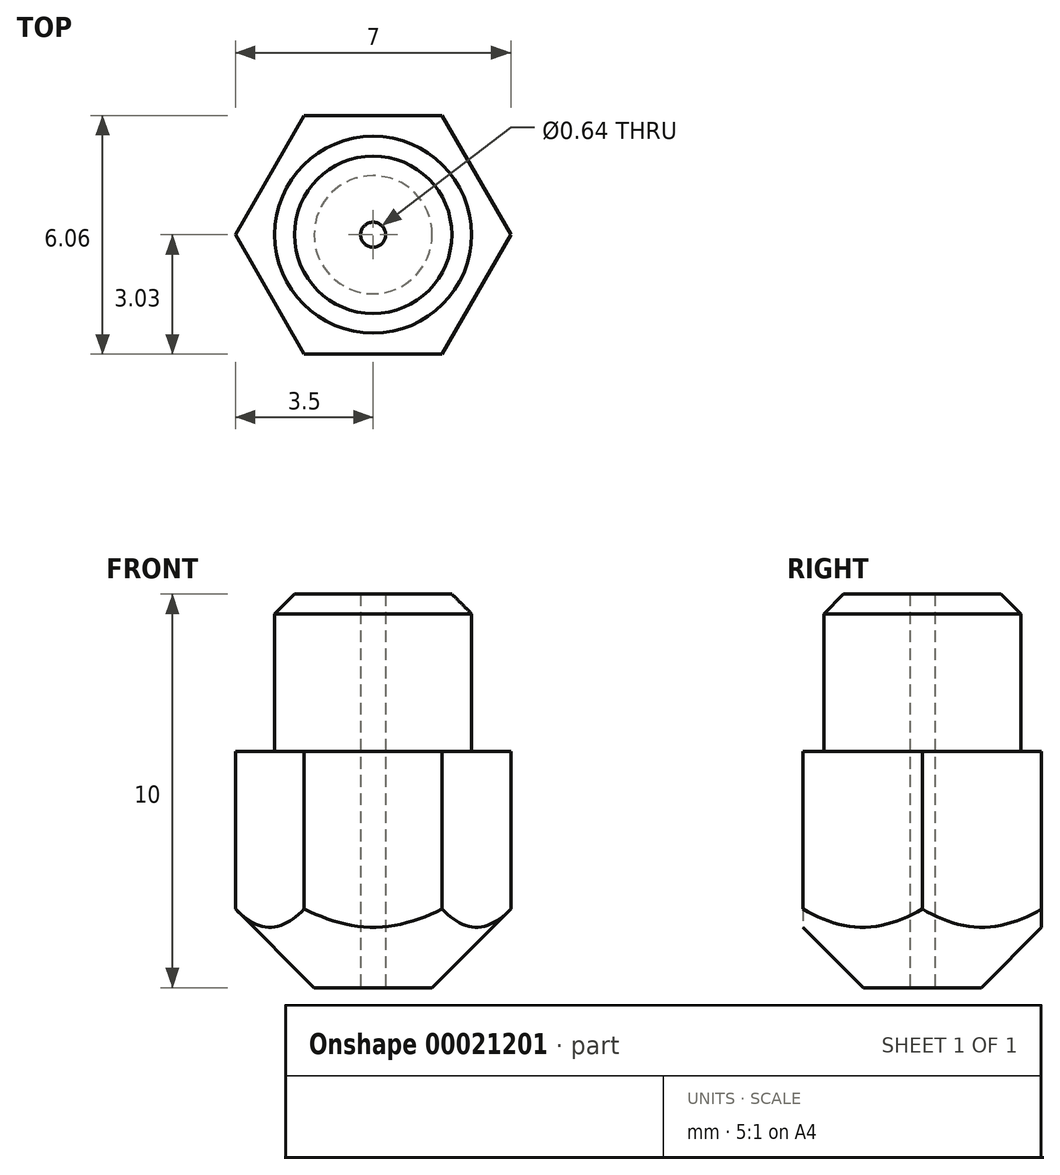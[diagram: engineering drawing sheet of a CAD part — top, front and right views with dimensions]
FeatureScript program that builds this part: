
annotation { "Feature Type Name" : "Feature", "Feature Type Description" : "" }
export const myFeature = defineFeature(function(context is Context, id is Id, definition is map)
    precondition{}
    {
        {
            var Q0;
            Q0=qCreatedBy(makeId("Top.planeOp"),FACE);
            var sketch = newSketch(context, id + "F0", { "sketchPlane" : qUnion([Q0])});
            skCircle(sketch, "E0.cCircle", {"center": v(0, 0) * mm, "radius": 3.03 * mm, "construction": true});
            skLineSegment(sketch, "E0.0", {"start": v(1.75, -3.03) * mm, "end": v(-1.75, -3.03) * mm});
            skLineSegment(sketch, "E0.1", {"start": v(-1.75, -3.03) * mm, "end": v(-3.5, 0) * mm});
            skLineSegment(sketch, "E0.2", {"start": v(-3.5, 0) * mm, "end": v(-1.75, 3.03) * mm});
            skLineSegment(sketch, "E0.3", {"start": v(-1.75, 3.03) * mm, "end": v(1.75, 3.03) * mm});
            skLineSegment(sketch, "E0.4", {"start": v(1.75, 3.03) * mm, "end": v(3.5, 0) * mm});
            skLineSegment(sketch, "E0.5", {"start": v(3.5, 0) * mm, "end": v(1.75, -3.03) * mm});
            skPoint(sketch, "E0.0.midPoint", {"position": v(0, -3.03) * mm});
            skSolve(sketch);
        }
        {
            var Q0;
            Q0=qSketchRegion(id+"F0",true);
            extrude(context, id + "F1", {"entities" : qUnion([Q0]), "depth" : 6 * mm});
        }
        {
            var Q0;
            Q0=qCreatedBy(makeId("Front.planeOp"),FACE);
            var sketch = newSketch(context, id + "F2", { "sketchPlane" : qUnion([Q0])});
            skLineSegment(sketch, "E1", {"start": v(1.5, 0) * mm, "end": v(3.5, 2) * mm});
            skLineSegment(sketch, "E2", {"start": v(3.5, 2) * mm, "end": v(3.5, 0) * mm});
            skLineSegment(sketch, "E3", {"start": v(3.5, 0) * mm, "end": v(1.5, 0) * mm});
            skLineSegment(sketch, "E4", {"start": v(0, 0) * mm, "end": v(0, 3.2) * mm, "construction": true});
            skSolve(sketch);
        }
        {
            var Q0;
            Q0=qSketchRegion(id+"F2",true);
            var Q1;
            Q1=sQuery(id+"F2.wireOp",EDGE,"E4");
            revolve(context, id + "F3", {"operationType" : NewBodyOperationType.REMOVE, "entities" : qUnion([Q0]), "axis" : qUnion([Q1]), "revolveType" : RevolveType.FULL, "oppositeDirection" : true});
        }
        {
            var Q0;
            Q0=makeQuery(id+"F1.opExtrude","CAP_FACE",FACE,{"disambiguationData":[OSD([sQuery(id+"F0.wireOp",EDGE,"E0.0"),sQuery(id+"F0.wireOp",EDGE,"E0.1"),sQuery(id+"F0.wireOp",EDGE,"E0.2"),sQuery(id+"F0.wireOp",EDGE,"E0.3"),sQuery(id+"F0.wireOp",EDGE,"E0.4"),sQuery(id+"F0.wireOp",EDGE,"E0.5")])],"isStart":false});
            var sketch = newSketch(context, id + "F4", { "sketchPlane" : qUnion([Q0])});
            skCircle(sketch, "E5", {"center": v(0, 0) * mm, "radius": 2.5 * mm});
            skSolve(sketch);
        }
        {
            var Q0;
            Q0=qSketchRegion(id+"F4",true);
            extrude(context, id + "F5", {"entities" : qUnion([Q0]), "operationType" : NewBodyOperationType.ADD, "depth" : 4 * mm});
        }
        {
            var Q0;
            Q0=makeQuery(id+"F5.opExtrude","CAP_EDGE",EDGE,{"disambiguationData":[OSD([sQuery(id+"F4.wireOp",EDGE,"E5")])],"isStart":false});
            chamfer(context, id + "F6", {"entities" : qUnion([Q0]), "width" : 0.5 * mm, "tangentPropagation" : true});
        }
        {
            var Q0;
            Q0=makeQuery(id+"F1.opExtrude","CAP_FACE",FACE,{"disambiguationData":[OSD([sQuery(id+"F0.wireOp",EDGE,"E0.0"),sQuery(id+"F0.wireOp",EDGE,"E0.1"),sQuery(id+"F0.wireOp",EDGE,"E0.2"),sQuery(id+"F0.wireOp",EDGE,"E0.3"),sQuery(id+"F0.wireOp",EDGE,"E0.4"),sQuery(id+"F0.wireOp",EDGE,"E0.5")])],"isStart":true});
            var sketch = newSketch(context, id + "F7", { "sketchPlane" : qUnion([Q0])});
            skCircle(sketch, "E6", {"center": v(0, 0) * mm, "radius": 0.32 * mm});
            skSolve(sketch);
        }
        {
            var Q0;
            Q0=qSketchRegion(id+"F7",true);
            extrude(context, id + "F8", {"entities" : qUnion([Q0]), "operationType" : NewBodyOperationType.REMOVE, "endBound" : BoundingType.THROUGH_ALL, "oppositeDirection" : true, "depth" : 25 * mm});
        }
    });
